# Revit family: Sanext_Тройник с внутренней резьбой
name_source: partatom
category: Соединительные детали трубопроводов
revit_build: Autodesk Revit 2017 (Build: 20160225_1515(x64)
units: mm (PartAtom-declared; Revit-internal decimal feet)

## family parameters
Всегда вертикально = Да
На основе рабочей плоскости = Нет
Общий = Нет
При загрузке вырезать с полостями = Нет
Размер круглого соединителя = Использовать радиус
Тип детали = Тройник

## types (4) — shared parameters
ADSK_Единица измерения = шт
ADSK_Завод-изготовитель = Sanext
URL = http://sanext.ru
Изготовитель = Sanext
Материал фитинга = DZR латунь
Разработчик = ООО ПРОРУБИМ
Разработчик (телефон) = +7(495)649-85-43
Разработчик модели (URL) = http://prorubim.com
zero-valued in all types: ADSK_Масса

## per-type parameters (varying)
| type | ADSK_Код изделия | DN1 | DN2 | DN3 | L | R1 | R2 | R3 | a | b | c |
| Тройник с врнутренней резьбой 32xG1x32 | 4676 | 32 мм | 32 мм | 32 мм | 140 мм | 16 мм | 16 мм | 16 мм | 70 мм | 30 мм | 70 мм |
| Тройник с врнутренней резьбой 25xG3/4"x25 | 4675 | 25 мм | 25 мм | 25 мм | 120 мм | 13 мм | 13 мм | 13 мм | 60 мм | 26 мм | 60 мм |
| Тройник с врнутренней резьбой 20xG1/2"x20 | 4915 | 20 мм | 20 мм | 20 мм | 98 мм | 10 мм | 10 мм | 10 мм | 49 мм | 24 мм | 49 мм |
| Тройник с врнутренней резьбой 16x1/2"x16 | 4914 | 16 мм | 16 мм | 20 мм | 88 мм | 8 мм | 8 мм | 10 мм | 44 мм | 24 мм | 44 мм |

note: column(s) folded — value = type name in every type: ADSK_Наименование
